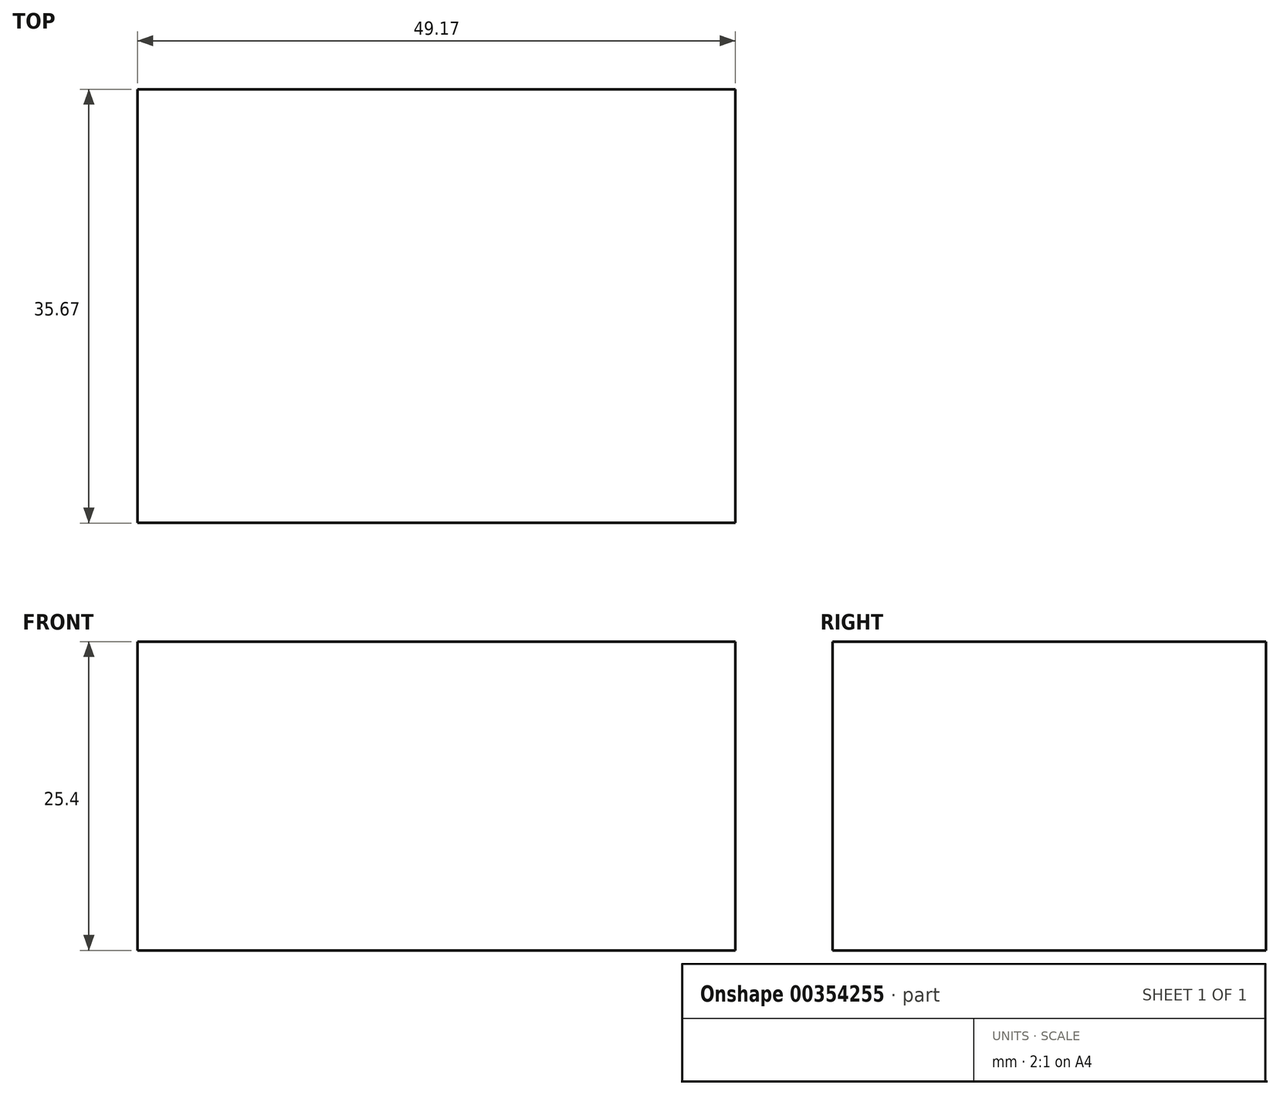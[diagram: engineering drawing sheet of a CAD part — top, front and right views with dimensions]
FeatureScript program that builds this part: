
annotation { "Feature Type Name" : "Feature", "Feature Type Description" : "" }
export const myFeature = defineFeature(function(context is Context, id is Id, definition is map)
    precondition{}
    {
        {
            var Q0;
            Q0=qCreatedBy(makeId("Top.planeOp"),FACE);
            var sketch = newSketch(context, id + "F0", { "sketchPlane" : qUnion([Q0])});
            skLineSegment(sketch, "E0.bottom", {"start": v(0, 77.6) * mm, "end": v(49.17, 77.6) * mm});
            skLineSegment(sketch, "E0.top", {"start": v(0, 41.93) * mm, "end": v(49.17, 41.93) * mm});
            skLineSegment(sketch, "E0.left", {"start": v(0, 77.6) * mm, "end": v(0, 41.93) * mm});
            skLineSegment(sketch, "E0.right", {"start": v(49.17, 77.6) * mm, "end": v(49.17, 41.93) * mm});
            skSolve(sketch);
        }
        {
            var Q0;
            Q0 = qSketchRegion(id + "F0", true);
            extrude(context, id + "F1", {"entities" : qUnion([Q0]), "depth" : 25.4 * mm});
        }
    });
